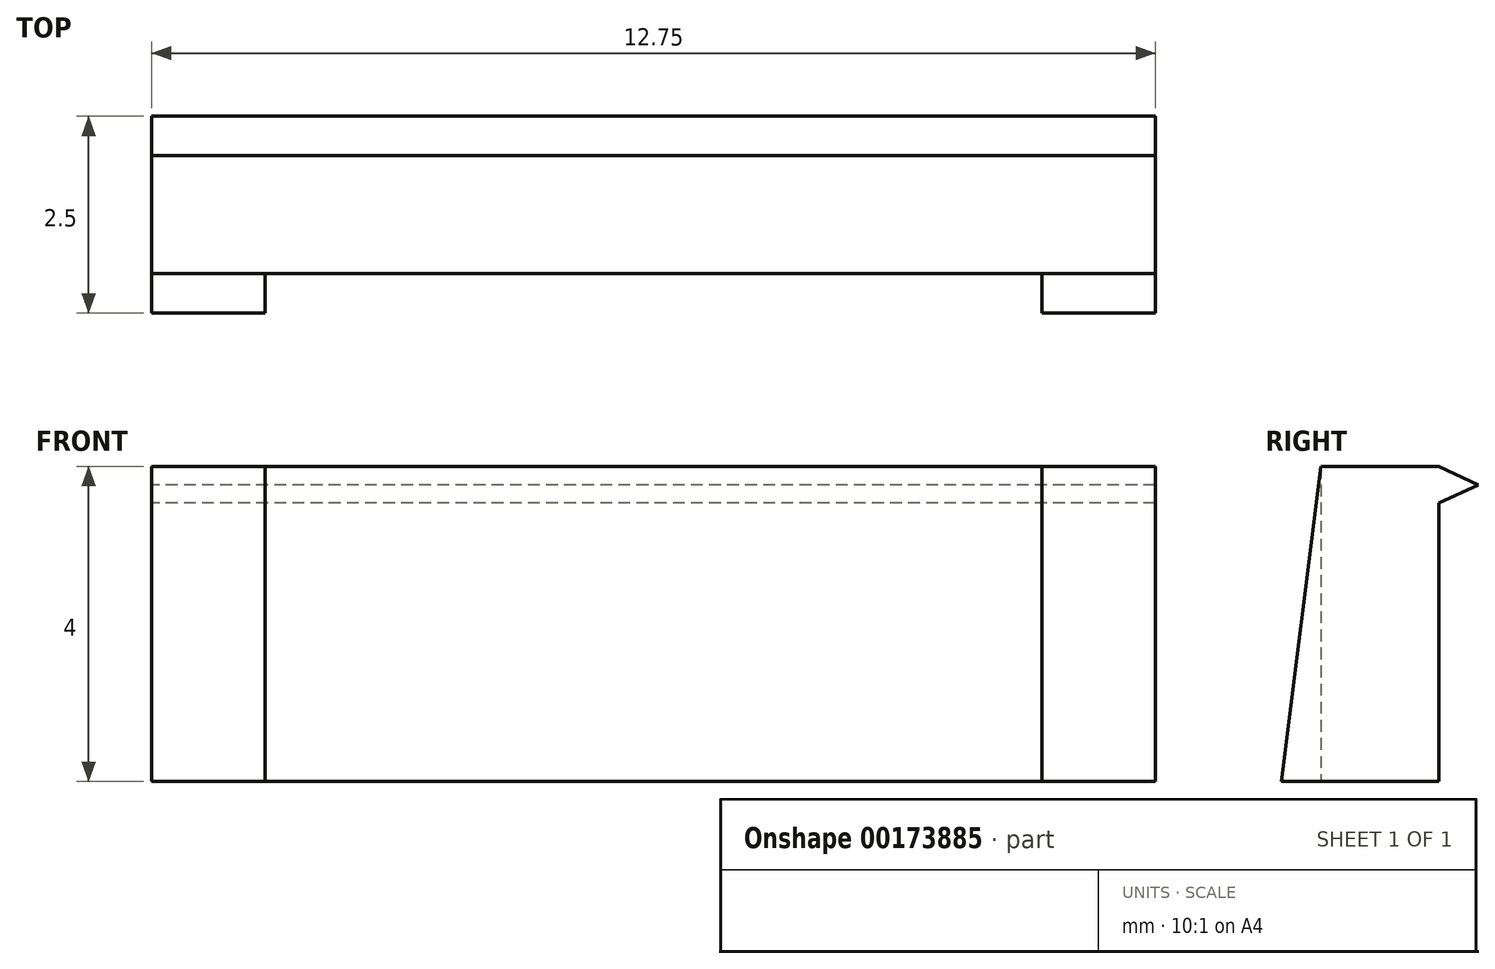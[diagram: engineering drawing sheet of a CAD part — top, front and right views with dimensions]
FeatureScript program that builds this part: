
annotation { "Feature Type Name" : "Feature", "Feature Type Description" : "" }
export const myFeature = defineFeature(function(context is Context, id is Id, definition is map)
    precondition{}
    {
        {
            var Q0;
            Q0=qCreatedBy(makeId("Right.planeOp"),FACE);
            var sketch = newSketch(context, id + "F0", { "sketchPlane" : qUnion([Q0])});
            skLineSegment(sketch, "E0", {"start": v(0, 4) * mm, "end": v(1.5, 4) * mm});
            skLineSegment(sketch, "E1", {"start": v(1.5, 4) * mm, "end": v(2, 3.77) * mm});
            skLineSegment(sketch, "E2", {"start": v(2, 3.77) * mm, "end": v(1.5, 3.53) * mm});
            skLineSegment(sketch, "E3", {"start": v(1.5, 3.53) * mm, "end": v(1.5, 0) * mm});
            skLineSegment(sketch, "E4", {"start": v(1.5, 0) * mm, "end": v(-0.5, 0) * mm});
            skLineSegment(sketch, "E5", {"start": v(-0.5, 0) * mm, "end": v(0, 4) * mm});
            skSolve(sketch);
        }
        {
            var Q0;
            Q0 = qSketchRegion(id + "F0", true);
            extrude(context, id + "F1", {"entities" : qUnion([Q0]), "depth" : 12.75 * mm});
        }
        {
            var Q0;
            Q0=makeQuery(id+"F1.opExtrude","SWEPT_FACE",FACE,{"disambiguationData":[OSD([sQuery(id+"F0.wireOp",EDGE,"E4")])]});
            var sketch = newSketch(context, id + "F2", { "sketchPlane" : qUnion([Q0])});
            skLineSegment(sketch, "E6.bottom", {"start": v(1.44, 0.5) * mm, "end": v(11.3, 0.5) * mm});
            skLineSegment(sketch, "E6.top", {"start": v(1.44, 0) * mm, "end": v(11.3, 0) * mm});
            skLineSegment(sketch, "E6.left", {"start": v(1.44, 0.5) * mm, "end": v(1.44, 0) * mm});
            skLineSegment(sketch, "E6.right", {"start": v(11.3, 0.5) * mm, "end": v(11.3, 0) * mm});
            skSolve(sketch);
        }
        {
            var Q0;
            Q0 = qSketchRegion(id + "F2", true);
            extrude(context, id + "F3", {"entities" : qUnion([Q0]), "operationType" : NewBodyOperationType.REMOVE, "endBound" : BoundingType.THROUGH_ALL, "oppositeDirection" : true, "depth" : 25 * mm});
        }
    });
